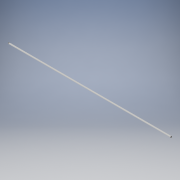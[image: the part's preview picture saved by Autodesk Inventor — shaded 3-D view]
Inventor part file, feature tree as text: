
AUTODESK INVENTOR PART (.ipt)
format: ipt  version: 2019 (Build 230136000, 136)  size: 94,208 bytes
history: native  units: in
note: dims shown in document units (in); Inventor stores cm internally (conversion verified against a paired STEP export)
features: extrude x1, sketch x1
ambient origin geometry x8: Origin, YZ Plane, XZ Plane, XY Plane, X Axis, Y Axis, Z Axis, Center Point
bodies: Solid1 (feature_tree)
feature tree (2):
  extrude  "Extrusion1"  Depth=39.3701in TaperAngle=0.0deg
  sketch  "Sketch1"  dims[d0=0.315in d1=39.3701in d2=0.0in]
